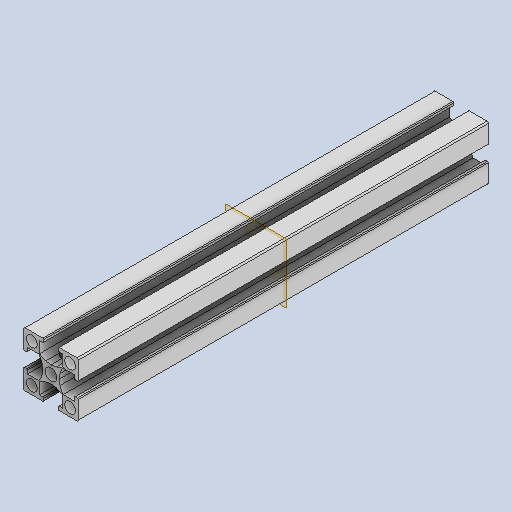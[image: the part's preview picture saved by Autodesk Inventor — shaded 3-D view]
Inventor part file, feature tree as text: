
AUTODESK INVENTOR PART (.ipt)
format: ipt  version: 2024 (Build 280153000, 153)  size: 270,848 bytes
history: native  units: in
note: dims shown in document units (in); Inventor stores cm internally (conversion verified against a paired STEP export)
features: extrude x2, sketch x2, plane x1
ambient origin geometry x8: Origin, YZ Plane, XZ Plane, XY Plane, X Axis, Y Axis, Z Axis, Center Point
bodies: Solid1 (feature_tree)
feature tree (5):
  extrude  "Extrusion1"  Depth=0.1693in
  extrude  "Extrusion2"  Depth=0.3937in TaperAngle=360.0deg
  plane  "Work Plane1"
  sketch  "Sketch1"  dims[d1=45.0deg d2=0.1693in]
  sketch  "Sketch2"  dims[d3=0.1575in d4=1.5748in d6=360.0deg d9=0.1043in d10=0.1654in d11=0.0551in d12=0.2756in d13=0.3937in d14=0.3937in d15=0.0551in d16=0.1043in d18=0.0118in d19=0.0197in d21=0.2756in d22=0.1654in d23=0.2756in d24=0.2638in d25=0.0118in d26=0.2756in d27=0.2638in d28=0.0118in d29=0.2756in d30=1.5748in d32=360.0deg d34=5.9055in d35=0.0in d36=0.1693in d37=0.2362in d38=0.3937in d39=0.0in]
